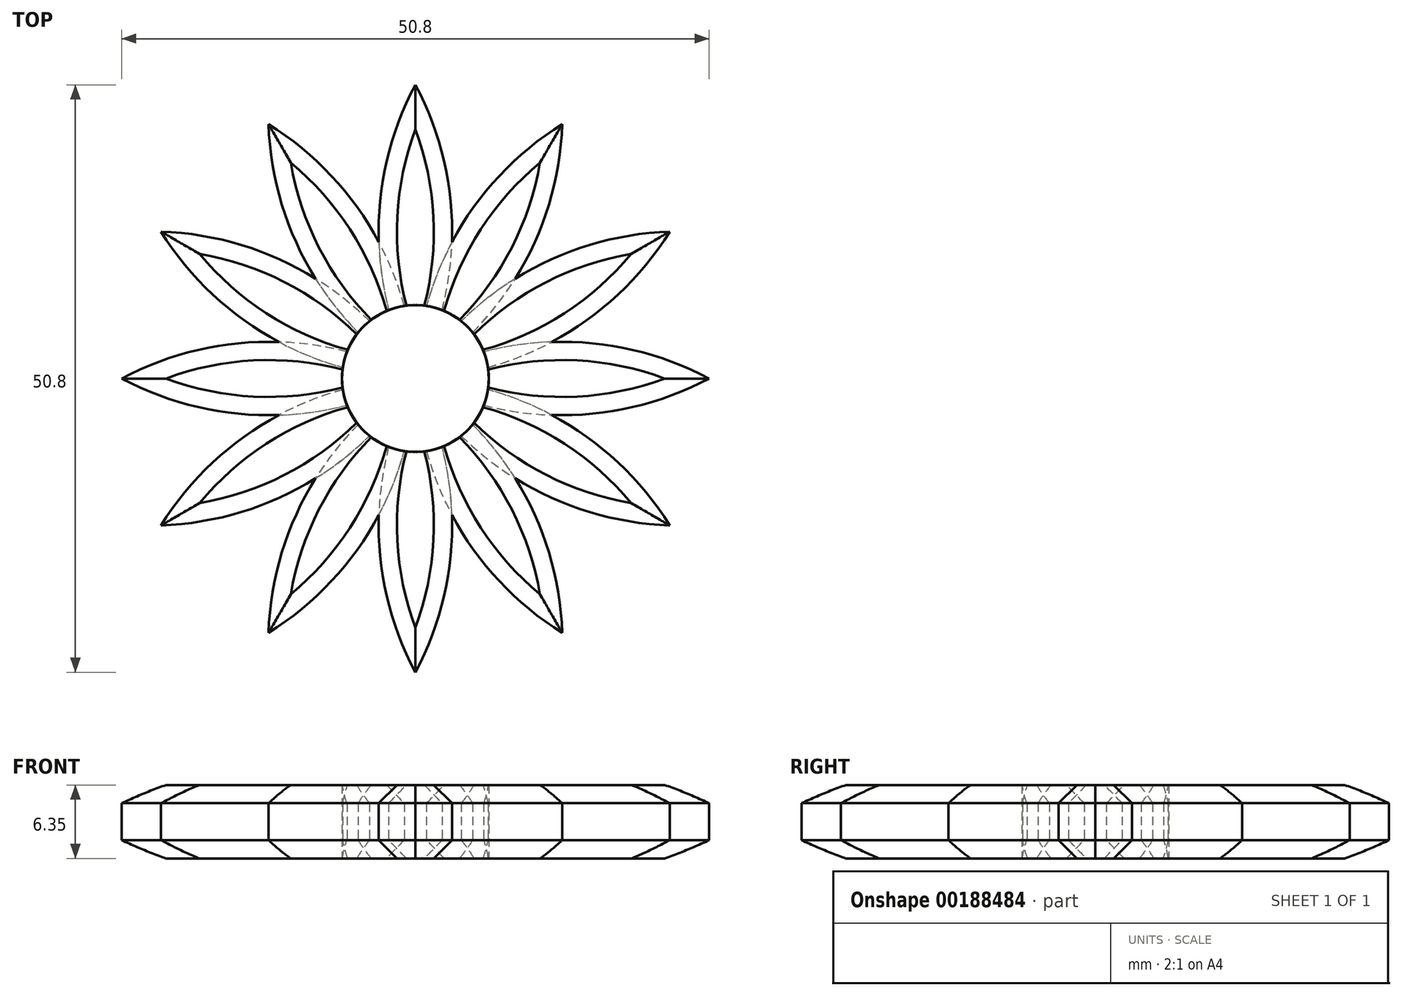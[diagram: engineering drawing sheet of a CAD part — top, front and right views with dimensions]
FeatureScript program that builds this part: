
annotation { "Feature Type Name" : "Feature", "Feature Type Description" : "" }
export const myFeature = defineFeature(function(context is Context, id is Id, definition is map)
    precondition{}
    {
        {
            var Q0;
            Q0=qCreatedBy(makeId("Top.planeOp"),FACE);
            var sketch = newSketch(context, id + "F0", { "sketchPlane" : qUnion([Q0])});
            skLineSegment(sketch, "E0", {"start": v(0, 0) * mm, "end": v(0, 25.4) * mm});
            skArc(sketch, "E1", {"start": v(0, 0) * mm, "mid": v(3.18, 12.7) * mm, "end": v(0, 25.4) * mm});
            skArc(sketch, "E2", {"start": v(0, 25.4) * mm, "mid": v(-3.18, 12.7) * mm, "end": v(0, 0) * mm});
            skSolve(sketch);
        }
        {
            var Q0;
            Q0 = qSketchRegion(id + "F0", true);
            extrude(context, id + "F1", {"entities" : qUnion([Q0]), "depth" : 6.35 * mm});
        }
        {
            var Q0;
            Q0=makeQuery(id+"F1.opExtrude","CAP_EDGE",EDGE,{"disambiguationData":[OSD([sQuery(id+"F0.wireOp",EDGE,"E1")])],"isStart":false});
            var Q1;
            Q1=makeQuery(id+"F1.opExtrude","CAP_EDGE",EDGE,{"disambiguationData":[OSD([sQuery(id+"F0.wireOp",EDGE,"E2")])],"isStart":false});
            var Q2;
            Q2=makeQuery(id+"F1.opExtrude","CAP_EDGE",EDGE,{"disambiguationData":[OSD([sQuery(id+"F0.wireOp",EDGE,"E1")])],"isStart":true});
            var Q3;
            Q3=makeQuery(id+"F1.opExtrude","CAP_EDGE",EDGE,{"disambiguationData":[OSD([sQuery(id+"F0.wireOp",EDGE,"E2")])],"isStart":true});
            chamfer(context, id + "F2", {"entities" : qUnion([Q0, Q1, Q2, Q3]), "width" : 1.58 * mm, "tangentPropagation" : true});
        }
        {
            var Q0;
            Q0=qCreatedBy(makeId("Top.planeOp"),FACE);
            var sketch = newSketch(context, id + "F3", { "sketchPlane" : qUnion([Q0])});
            skCircle(sketch, "E3", {"center": v(0, 0) * mm, "radius": 6.35 * mm});
            skSolve(sketch);
        }
        {
            var Q0;
            Q0=makeQuery(id+"F3.imprint","IMPRINT",FACE,{"disambiguationData":[TD([[makeQuery(id+"F3.imprint","IMPRINT",EDGE,{"derivedFrom":sQuery(id+"F3.wireOp",EDGE,"E3")}),1.0]])]});
            extrude(context, id + "F4", {"entities" : qUnion([Q0]), "operationType" : NewBodyOperationType.ADD, "depth" : 6.35 * mm});
        }
        {
            var Q0;
            Q0=makeQuery(id+"F1.opExtrude","SWEPT_BODY",BODY,{"disambiguationData":[OSD([sQuery(id+"F0.wireOp",EDGE,"E1"),sQuery(id+"F0.wireOp",EDGE,"E2")])]});
            var Q1;
            Q1=makeQuery(id+"F4.opExtrude","SWEPT_FACE",FACE,{"disambiguationData":[OSD([sQuery(id+"F3.wireOp",EDGE,"E3")])]});
            circularPattern(context, id + "F5", {"entities" : qUnion([Q0]), "axis" : qUnion([Q1]), "angle" : 30 * degree, "instanceCount" : 14, "oppositeDirection" : true});
        }
    });
